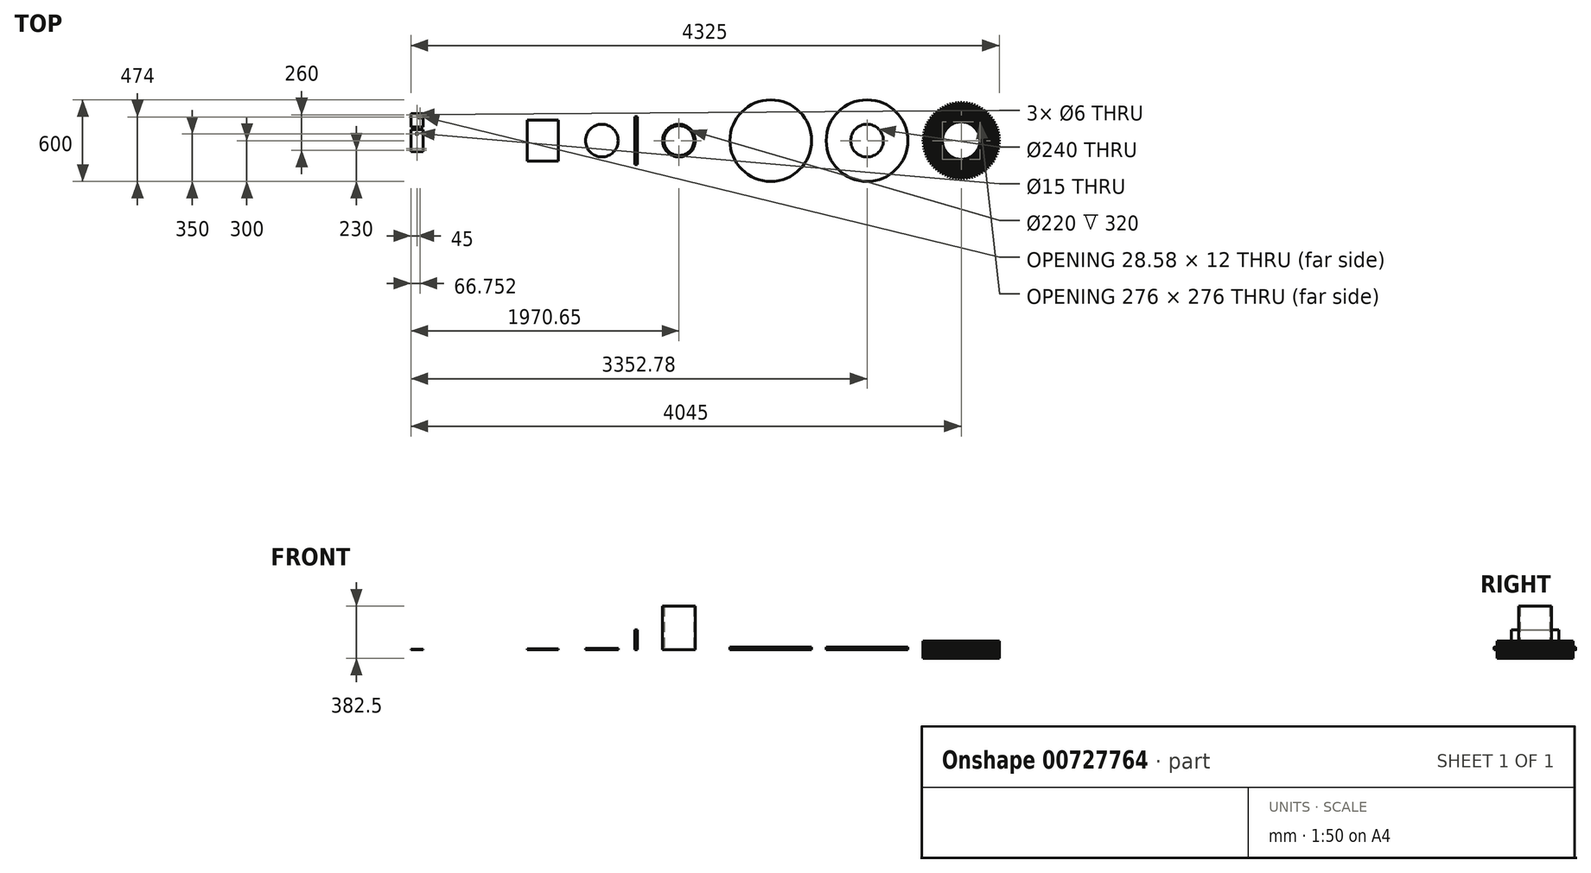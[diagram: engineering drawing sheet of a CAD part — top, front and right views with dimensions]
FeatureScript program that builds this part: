
annotation { "Feature Type Name" : "Feature", "Feature Type Description" : "" }
export const myFeature = defineFeature(function(context is Context, id is Id, definition is map)
    precondition{}
    {
        {
            var Q0;
            Q0=qCreatedBy(makeId("Top.planeOp"),FACE);
            var sketch = newSketch(context, id + "F0", { "sketchPlane" : qUnion([Q0])});
            skLineSegment(sketch, "E0.bottom", {"start": v(138, -5) * mm, "end": v(280, -5) * mm});
            skLineSegment(sketch, "E0.top", {"start": v(138, 5) * mm, "end": v(280, 5) * mm});
            skLineSegment(sketch, "E0.left", {"start": v(138, -5) * mm, "end": v(138, 5) * mm});
            skLineSegment(sketch, "E0.right", {"start": v(280, -5) * mm, "end": v(280, 5) * mm});
            skPoint(sketch, "E0.middle", {"position": v(209, 0) * mm});
            skLineSegment(sketch, "E1.1.0", {"start": v(137.3, 14.83) * mm, "end": v(278.93, 24.96) * mm});
            skLineSegment(sketch, "E1.1.1", {"start": v(138, 4.86) * mm, "end": v(137.3, 14.83) * mm});
            skLineSegment(sketch, "E1.1.2", {"start": v(138, 4.86) * mm, "end": v(279.64, 14.99) * mm});
            skLineSegment(sketch, "E1.1.3", {"start": v(279.64, 14.99) * mm, "end": v(278.93, 24.96) * mm});
            skLineSegment(sketch, "E1.2.0", {"start": v(135.88, 24.59) * mm, "end": v(276.44, 44.8) * mm});
            skLineSegment(sketch, "E1.2.1", {"start": v(137.3, 14.7) * mm, "end": v(135.88, 24.59) * mm});
            skLineSegment(sketch, "E1.2.2", {"start": v(137.3, 14.7) * mm, "end": v(277.86, 34.9) * mm});
            skLineSegment(sketch, "E1.2.3", {"start": v(277.86, 34.9) * mm, "end": v(276.44, 44.8) * mm});
            skLineSegment(sketch, "E1.3.0", {"start": v(133.78, 34.22) * mm, "end": v(272.54, 64.4) * mm});
            skLineSegment(sketch, "E1.3.1", {"start": v(135.9, 24.45) * mm, "end": v(133.78, 34.22) * mm});
            skLineSegment(sketch, "E1.3.2", {"start": v(135.9, 24.45) * mm, "end": v(274.66, 54.63) * mm});
            skLineSegment(sketch, "E1.3.3", {"start": v(274.66, 54.63) * mm, "end": v(272.54, 64.4) * mm});
            skLineSegment(sketch, "E1.4.0", {"start": v(131, 43.68) * mm, "end": v(267.25, 83.68) * mm});
            skLineSegment(sketch, "E1.4.1", {"start": v(133.82, 34.08) * mm, "end": v(131, 43.68) * mm});
            skLineSegment(sketch, "E1.4.2", {"start": v(133.82, 34.08) * mm, "end": v(270.07, 74.09) * mm});
            skLineSegment(sketch, "E1.4.3", {"start": v(270.07, 74.09) * mm, "end": v(267.25, 83.68) * mm});
            skLineSegment(sketch, "E1.5.0", {"start": v(127.55, 52.91) * mm, "end": v(260.6, 102.53) * mm});
            skLineSegment(sketch, "E1.5.1", {"start": v(131.05, 43.54) * mm, "end": v(127.55, 52.91) * mm});
            skLineSegment(sketch, "E1.5.2", {"start": v(131.05, 43.54) * mm, "end": v(264.1, 93.17) * mm});
            skLineSegment(sketch, "E1.5.3", {"start": v(264.1, 93.17) * mm, "end": v(260.6, 102.53) * mm});
            skLineSegment(sketch, "E1.6.0", {"start": v(123.45, 61.88) * mm, "end": v(252.62, 120.86) * mm});
            skLineSegment(sketch, "E1.6.1", {"start": v(127.6, 52.78) * mm, "end": v(123.45, 61.88) * mm});
            skLineSegment(sketch, "E1.6.2", {"start": v(127.6, 52.78) * mm, "end": v(256.77, 111.77) * mm});
            skLineSegment(sketch, "E1.6.3", {"start": v(256.77, 111.77) * mm, "end": v(252.62, 120.86) * mm});
            skLineSegment(sketch, "E1.7.0", {"start": v(118.72, 70.52) * mm, "end": v(243.35, 138.58) * mm});
            skLineSegment(sketch, "E1.7.1", {"start": v(123.52, 61.75) * mm, "end": v(118.72, 70.52) * mm});
            skLineSegment(sketch, "E1.7.2", {"start": v(123.52, 61.75) * mm, "end": v(248.15, 129.8) * mm});
            skLineSegment(sketch, "E1.7.3", {"start": v(248.15, 129.8) * mm, "end": v(243.35, 138.58) * mm});
            skLineSegment(sketch, "E1.8.0", {"start": v(113.39, 78.81) * mm, "end": v(232.85, 155.59) * mm});
            skLineSegment(sketch, "E1.8.1", {"start": v(118.8, 70.4) * mm, "end": v(113.39, 78.81) * mm});
            skLineSegment(sketch, "E1.8.2", {"start": v(118.8, 70.4) * mm, "end": v(238.25, 147.17) * mm});
            skLineSegment(sketch, "E1.8.3", {"start": v(238.25, 147.17) * mm, "end": v(232.85, 155.59) * mm});
            skLineSegment(sketch, "E1.9.0", {"start": v(107.48, 86.7) * mm, "end": v(221.16, 171.8) * mm});
            skLineSegment(sketch, "E1.9.1", {"start": v(113.47, 78.7) * mm, "end": v(107.48, 86.7) * mm});
            skLineSegment(sketch, "E1.9.2", {"start": v(113.47, 78.7) * mm, "end": v(227.15, 163.8) * mm});
            skLineSegment(sketch, "E1.9.3", {"start": v(227.15, 163.8) * mm, "end": v(221.16, 171.8) * mm});
            skLineSegment(sketch, "E1.10.0", {"start": v(101.02, 94.15) * mm, "end": v(208.34, 187.14) * mm});
            skLineSegment(sketch, "E1.10.1", {"start": v(107.57, 86.6) * mm, "end": v(101.02, 94.15) * mm});
            skLineSegment(sketch, "E1.10.2", {"start": v(107.57, 86.6) * mm, "end": v(214.88, 179.58) * mm});
            skLineSegment(sketch, "E1.10.3", {"start": v(214.88, 179.58) * mm, "end": v(208.34, 187.14) * mm});
            skLineSegment(sketch, "E1.11.0", {"start": v(94.05, 101.12) * mm, "end": v(194.45, 201.53) * mm});
            skLineSegment(sketch, "E1.11.1", {"start": v(101.12, 94.05) * mm, "end": v(94.05, 101.12) * mm});
            skLineSegment(sketch, "E1.11.2", {"start": v(101.12, 94.05) * mm, "end": v(201.53, 194.45) * mm});
            skLineSegment(sketch, "E1.11.3", {"start": v(201.53, 194.45) * mm, "end": v(194.45, 201.53) * mm});
            skLineSegment(sketch, "E1.12.0", {"start": v(86.6, 107.57) * mm, "end": v(179.58, 214.88) * mm});
            skLineSegment(sketch, "E1.12.1", {"start": v(94.15, 101.02) * mm, "end": v(86.6, 107.57) * mm});
            skLineSegment(sketch, "E1.12.2", {"start": v(94.15, 101.02) * mm, "end": v(187.14, 208.34) * mm});
            skLineSegment(sketch, "E1.12.3", {"start": v(187.14, 208.34) * mm, "end": v(179.58, 214.88) * mm});
            skLineSegment(sketch, "E1.13.0", {"start": v(78.7, 113.47) * mm, "end": v(163.8, 227.15) * mm});
            skLineSegment(sketch, "E1.13.1", {"start": v(86.7, 107.48) * mm, "end": v(78.7, 113.47) * mm});
            skLineSegment(sketch, "E1.13.2", {"start": v(86.7, 107.48) * mm, "end": v(171.8, 221.16) * mm});
            skLineSegment(sketch, "E1.13.3", {"start": v(171.8, 221.16) * mm, "end": v(163.8, 227.15) * mm});
            skLineSegment(sketch, "E1.14.0", {"start": v(70.4, 118.8) * mm, "end": v(147.17, 238.25) * mm});
            skLineSegment(sketch, "E1.14.1", {"start": v(78.81, 113.39) * mm, "end": v(70.4, 118.8) * mm});
            skLineSegment(sketch, "E1.14.2", {"start": v(78.81, 113.39) * mm, "end": v(155.59, 232.85) * mm});
            skLineSegment(sketch, "E1.14.3", {"start": v(155.59, 232.85) * mm, "end": v(147.17, 238.25) * mm});
            skLineSegment(sketch, "E1.15.0", {"start": v(61.75, 123.52) * mm, "end": v(129.8, 248.15) * mm});
            skLineSegment(sketch, "E1.15.1", {"start": v(70.52, 118.72) * mm, "end": v(61.75, 123.52) * mm});
            skLineSegment(sketch, "E1.15.2", {"start": v(70.52, 118.72) * mm, "end": v(138.58, 243.35) * mm});
            skLineSegment(sketch, "E1.15.3", {"start": v(138.58, 243.35) * mm, "end": v(129.8, 248.15) * mm});
            skLineSegment(sketch, "E1.16.0", {"start": v(52.78, 127.6) * mm, "end": v(111.77, 256.77) * mm});
            skLineSegment(sketch, "E1.16.1", {"start": v(61.88, 123.45) * mm, "end": v(52.78, 127.6) * mm});
            skLineSegment(sketch, "E1.16.2", {"start": v(61.88, 123.45) * mm, "end": v(120.86, 252.62) * mm});
            skLineSegment(sketch, "E1.16.3", {"start": v(120.86, 252.62) * mm, "end": v(111.77, 256.77) * mm});
            skLineSegment(sketch, "E1.17.0", {"start": v(43.54, 131.05) * mm, "end": v(93.17, 264.1) * mm});
            skLineSegment(sketch, "E1.17.1", {"start": v(52.91, 127.55) * mm, "end": v(43.54, 131.05) * mm});
            skLineSegment(sketch, "E1.17.2", {"start": v(52.91, 127.55) * mm, "end": v(102.53, 260.6) * mm});
            skLineSegment(sketch, "E1.17.3", {"start": v(102.53, 260.6) * mm, "end": v(93.17, 264.1) * mm});
            skLineSegment(sketch, "E1.18.0", {"start": v(34.08, 133.82) * mm, "end": v(74.09, 270.07) * mm});
            skLineSegment(sketch, "E1.18.1", {"start": v(43.68, 131) * mm, "end": v(34.08, 133.82) * mm});
            skLineSegment(sketch, "E1.18.2", {"start": v(43.68, 131) * mm, "end": v(83.68, 267.25) * mm});
            skLineSegment(sketch, "E1.18.3", {"start": v(83.68, 267.25) * mm, "end": v(74.09, 270.07) * mm});
            skLineSegment(sketch, "E1.19.0", {"start": v(24.45, 135.9) * mm, "end": v(54.63, 274.66) * mm});
            skLineSegment(sketch, "E1.19.1", {"start": v(34.22, 133.78) * mm, "end": v(24.45, 135.9) * mm});
            skLineSegment(sketch, "E1.19.2", {"start": v(34.22, 133.78) * mm, "end": v(64.4, 272.54) * mm});
            skLineSegment(sketch, "E1.19.3", {"start": v(64.4, 272.54) * mm, "end": v(54.63, 274.66) * mm});
            skLineSegment(sketch, "E1.20.0", {"start": v(14.7, 137.3) * mm, "end": v(34.9, 277.86) * mm});
            skLineSegment(sketch, "E1.20.1", {"start": v(24.59, 135.88) * mm, "end": v(14.7, 137.3) * mm});
            skLineSegment(sketch, "E1.20.2", {"start": v(24.59, 135.88) * mm, "end": v(44.8, 276.44) * mm});
            skLineSegment(sketch, "E1.20.3", {"start": v(44.8, 276.44) * mm, "end": v(34.9, 277.86) * mm});
            skLineSegment(sketch, "E1.21.0", {"start": v(4.86, 138) * mm, "end": v(14.99, 279.64) * mm});
            skLineSegment(sketch, "E1.21.1", {"start": v(14.83, 137.3) * mm, "end": v(4.86, 138) * mm});
            skLineSegment(sketch, "E1.21.2", {"start": v(14.83, 137.3) * mm, "end": v(24.96, 278.93) * mm});
            skLineSegment(sketch, "E1.21.3", {"start": v(24.96, 278.93) * mm, "end": v(14.99, 279.64) * mm});
            skLineSegment(sketch, "E1.22.0", {"start": v(-5, 138) * mm, "end": v(-5, 280) * mm});
            skLineSegment(sketch, "E1.22.1", {"start": v(5, 138) * mm, "end": v(-5, 138) * mm});
            skLineSegment(sketch, "E1.22.2", {"start": v(5, 138) * mm, "end": v(5, 280) * mm});
            skLineSegment(sketch, "E1.22.3", {"start": v(5, 280) * mm, "end": v(-5, 280) * mm});
            skLineSegment(sketch, "E1.23.0", {"start": v(-14.83, 137.3) * mm, "end": v(-24.96, 278.93) * mm});
            skLineSegment(sketch, "E1.23.1", {"start": v(-4.86, 138) * mm, "end": v(-14.83, 137.3) * mm});
            skLineSegment(sketch, "E1.23.2", {"start": v(-4.86, 138) * mm, "end": v(-14.99, 279.64) * mm});
            skLineSegment(sketch, "E1.23.3", {"start": v(-14.99, 279.64) * mm, "end": v(-24.96, 278.93) * mm});
            skLineSegment(sketch, "E1.24.0", {"start": v(-24.59, 135.88) * mm, "end": v(-44.8, 276.44) * mm});
            skLineSegment(sketch, "E1.24.1", {"start": v(-14.7, 137.3) * mm, "end": v(-24.59, 135.88) * mm});
            skLineSegment(sketch, "E1.24.2", {"start": v(-14.7, 137.3) * mm, "end": v(-34.9, 277.86) * mm});
            skLineSegment(sketch, "E1.24.3", {"start": v(-34.9, 277.86) * mm, "end": v(-44.8, 276.44) * mm});
            skLineSegment(sketch, "E1.25.0", {"start": v(-34.22, 133.78) * mm, "end": v(-64.4, 272.54) * mm});
            skLineSegment(sketch, "E1.25.1", {"start": v(-24.45, 135.9) * mm, "end": v(-34.22, 133.78) * mm});
            skLineSegment(sketch, "E1.25.2", {"start": v(-24.45, 135.9) * mm, "end": v(-54.63, 274.66) * mm});
            skLineSegment(sketch, "E1.25.3", {"start": v(-54.63, 274.66) * mm, "end": v(-64.4, 272.54) * mm});
            skLineSegment(sketch, "E1.26.0", {"start": v(-43.68, 131) * mm, "end": v(-83.68, 267.25) * mm});
            skLineSegment(sketch, "E1.26.1", {"start": v(-34.08, 133.82) * mm, "end": v(-43.68, 131) * mm});
            skLineSegment(sketch, "E1.26.2", {"start": v(-34.08, 133.82) * mm, "end": v(-74.09, 270.07) * mm});
            skLineSegment(sketch, "E1.26.3", {"start": v(-74.09, 270.07) * mm, "end": v(-83.68, 267.25) * mm});
            skLineSegment(sketch, "E1.27.0", {"start": v(-52.91, 127.55) * mm, "end": v(-102.53, 260.6) * mm});
            skLineSegment(sketch, "E1.27.1", {"start": v(-43.54, 131.05) * mm, "end": v(-52.91, 127.55) * mm});
            skLineSegment(sketch, "E1.27.2", {"start": v(-43.54, 131.05) * mm, "end": v(-93.17, 264.1) * mm});
            skLineSegment(sketch, "E1.27.3", {"start": v(-93.17, 264.1) * mm, "end": v(-102.53, 260.6) * mm});
            skLineSegment(sketch, "E1.28.0", {"start": v(-61.88, 123.45) * mm, "end": v(-120.86, 252.62) * mm});
            skLineSegment(sketch, "E1.28.1", {"start": v(-52.78, 127.6) * mm, "end": v(-61.88, 123.45) * mm});
            skLineSegment(sketch, "E1.28.2", {"start": v(-52.78, 127.6) * mm, "end": v(-111.77, 256.77) * mm});
            skLineSegment(sketch, "E1.28.3", {"start": v(-111.77, 256.77) * mm, "end": v(-120.86, 252.62) * mm});
            skLineSegment(sketch, "E1.29.0", {"start": v(-70.52, 118.72) * mm, "end": v(-138.58, 243.35) * mm});
            skLineSegment(sketch, "E1.29.1", {"start": v(-61.75, 123.52) * mm, "end": v(-70.52, 118.72) * mm});
            skLineSegment(sketch, "E1.29.2", {"start": v(-61.75, 123.52) * mm, "end": v(-129.8, 248.15) * mm});
            skLineSegment(sketch, "E1.29.3", {"start": v(-129.8, 248.15) * mm, "end": v(-138.58, 243.35) * mm});
            skLineSegment(sketch, "E1.30.0", {"start": v(-78.81, 113.39) * mm, "end": v(-155.59, 232.85) * mm});
            skLineSegment(sketch, "E1.30.1", {"start": v(-70.4, 118.8) * mm, "end": v(-78.81, 113.39) * mm});
            skLineSegment(sketch, "E1.30.2", {"start": v(-70.4, 118.8) * mm, "end": v(-147.17, 238.25) * mm});
            skLineSegment(sketch, "E1.30.3", {"start": v(-147.17, 238.25) * mm, "end": v(-155.59, 232.85) * mm});
            skLineSegment(sketch, "E1.31.0", {"start": v(-86.7, 107.48) * mm, "end": v(-171.8, 221.16) * mm});
            skLineSegment(sketch, "E1.31.1", {"start": v(-78.7, 113.47) * mm, "end": v(-86.7, 107.48) * mm});
            skLineSegment(sketch, "E1.31.2", {"start": v(-78.7, 113.47) * mm, "end": v(-163.8, 227.15) * mm});
            skLineSegment(sketch, "E1.31.3", {"start": v(-163.8, 227.15) * mm, "end": v(-171.8, 221.16) * mm});
            skLineSegment(sketch, "E1.32.0", {"start": v(-94.15, 101.02) * mm, "end": v(-187.14, 208.34) * mm});
            skLineSegment(sketch, "E1.32.1", {"start": v(-86.6, 107.57) * mm, "end": v(-94.15, 101.02) * mm});
            skLineSegment(sketch, "E1.32.2", {"start": v(-86.6, 107.57) * mm, "end": v(-179.58, 214.88) * mm});
            skLineSegment(sketch, "E1.32.3", {"start": v(-179.58, 214.88) * mm, "end": v(-187.14, 208.34) * mm});
            skLineSegment(sketch, "E1.33.0", {"start": v(-101.12, 94.05) * mm, "end": v(-201.53, 194.45) * mm});
            skLineSegment(sketch, "E1.33.1", {"start": v(-94.05, 101.12) * mm, "end": v(-101.12, 94.05) * mm});
            skLineSegment(sketch, "E1.33.2", {"start": v(-94.05, 101.12) * mm, "end": v(-194.45, 201.53) * mm});
            skLineSegment(sketch, "E1.33.3", {"start": v(-194.45, 201.53) * mm, "end": v(-201.53, 194.45) * mm});
            skLineSegment(sketch, "E1.34.0", {"start": v(-107.57, 86.6) * mm, "end": v(-214.88, 179.58) * mm});
            skLineSegment(sketch, "E1.34.1", {"start": v(-101.02, 94.15) * mm, "end": v(-107.57, 86.6) * mm});
            skLineSegment(sketch, "E1.34.2", {"start": v(-101.02, 94.15) * mm, "end": v(-208.34, 187.14) * mm});
            skLineSegment(sketch, "E1.34.3", {"start": v(-208.34, 187.14) * mm, "end": v(-214.88, 179.58) * mm});
            skLineSegment(sketch, "E1.35.0", {"start": v(-113.47, 78.7) * mm, "end": v(-227.15, 163.8) * mm});
            skLineSegment(sketch, "E1.35.1", {"start": v(-107.48, 86.7) * mm, "end": v(-113.47, 78.7) * mm});
            skLineSegment(sketch, "E1.35.2", {"start": v(-107.48, 86.7) * mm, "end": v(-221.16, 171.8) * mm});
            skLineSegment(sketch, "E1.35.3", {"start": v(-221.16, 171.8) * mm, "end": v(-227.15, 163.8) * mm});
            skLineSegment(sketch, "E1.36.0", {"start": v(-118.8, 70.4) * mm, "end": v(-238.25, 147.17) * mm});
            skLineSegment(sketch, "E1.36.1", {"start": v(-113.39, 78.81) * mm, "end": v(-118.8, 70.4) * mm});
            skLineSegment(sketch, "E1.36.2", {"start": v(-113.39, 78.81) * mm, "end": v(-232.85, 155.59) * mm});
            skLineSegment(sketch, "E1.36.3", {"start": v(-232.85, 155.59) * mm, "end": v(-238.25, 147.17) * mm});
            skLineSegment(sketch, "E1.37.0", {"start": v(-123.52, 61.75) * mm, "end": v(-248.15, 129.8) * mm});
            skLineSegment(sketch, "E1.37.1", {"start": v(-118.72, 70.52) * mm, "end": v(-123.52, 61.75) * mm});
            skLineSegment(sketch, "E1.37.2", {"start": v(-118.72, 70.52) * mm, "end": v(-243.35, 138.58) * mm});
            skLineSegment(sketch, "E1.37.3", {"start": v(-243.35, 138.58) * mm, "end": v(-248.15, 129.8) * mm});
            skLineSegment(sketch, "E1.38.0", {"start": v(-127.6, 52.78) * mm, "end": v(-256.77, 111.77) * mm});
            skLineSegment(sketch, "E1.38.1", {"start": v(-123.45, 61.88) * mm, "end": v(-127.6, 52.78) * mm});
            skLineSegment(sketch, "E1.38.2", {"start": v(-123.45, 61.88) * mm, "end": v(-252.62, 120.86) * mm});
            skLineSegment(sketch, "E1.38.3", {"start": v(-252.62, 120.86) * mm, "end": v(-256.77, 111.77) * mm});
            skLineSegment(sketch, "E1.39.0", {"start": v(-131.05, 43.54) * mm, "end": v(-264.1, 93.17) * mm});
            skLineSegment(sketch, "E1.39.1", {"start": v(-127.55, 52.91) * mm, "end": v(-131.05, 43.54) * mm});
            skLineSegment(sketch, "E1.39.2", {"start": v(-127.55, 52.91) * mm, "end": v(-260.6, 102.53) * mm});
            skLineSegment(sketch, "E1.39.3", {"start": v(-260.6, 102.53) * mm, "end": v(-264.1, 93.17) * mm});
            skLineSegment(sketch, "E1.40.0", {"start": v(-133.82, 34.08) * mm, "end": v(-270.07, 74.09) * mm});
            skLineSegment(sketch, "E1.40.1", {"start": v(-131, 43.68) * mm, "end": v(-133.82, 34.08) * mm});
            skLineSegment(sketch, "E1.40.2", {"start": v(-131, 43.68) * mm, "end": v(-267.25, 83.68) * mm});
            skLineSegment(sketch, "E1.40.3", {"start": v(-267.25, 83.68) * mm, "end": v(-270.07, 74.09) * mm});
            skLineSegment(sketch, "E1.41.0", {"start": v(-135.9, 24.45) * mm, "end": v(-274.66, 54.63) * mm});
            skLineSegment(sketch, "E1.41.1", {"start": v(-133.78, 34.22) * mm, "end": v(-135.9, 24.45) * mm});
            skLineSegment(sketch, "E1.41.2", {"start": v(-133.78, 34.22) * mm, "end": v(-272.54, 64.4) * mm});
            skLineSegment(sketch, "E1.41.3", {"start": v(-272.54, 64.4) * mm, "end": v(-274.66, 54.63) * mm});
            skLineSegment(sketch, "E1.42.0", {"start": v(-137.3, 14.7) * mm, "end": v(-277.86, 34.9) * mm});
            skLineSegment(sketch, "E1.42.1", {"start": v(-135.88, 24.59) * mm, "end": v(-137.3, 14.7) * mm});
            skLineSegment(sketch, "E1.42.2", {"start": v(-135.88, 24.59) * mm, "end": v(-276.44, 44.8) * mm});
            skLineSegment(sketch, "E1.42.3", {"start": v(-276.44, 44.8) * mm, "end": v(-277.86, 34.9) * mm});
            skLineSegment(sketch, "E1.43.0", {"start": v(-138, 4.86) * mm, "end": v(-279.64, 14.99) * mm});
            skLineSegment(sketch, "E1.43.1", {"start": v(-137.3, 14.83) * mm, "end": v(-138, 4.86) * mm});
            skLineSegment(sketch, "E1.43.2", {"start": v(-137.3, 14.83) * mm, "end": v(-278.93, 24.96) * mm});
            skLineSegment(sketch, "E1.43.3", {"start": v(-278.93, 24.96) * mm, "end": v(-279.64, 14.99) * mm});
            skLineSegment(sketch, "E1.44.0", {"start": v(-138, -5) * mm, "end": v(-280, -5) * mm});
            skLineSegment(sketch, "E1.44.1", {"start": v(-138, 5) * mm, "end": v(-138, -5) * mm});
            skLineSegment(sketch, "E1.44.2", {"start": v(-138, 5) * mm, "end": v(-280, 5) * mm});
            skLineSegment(sketch, "E1.44.3", {"start": v(-280, 5) * mm, "end": v(-280, -5) * mm});
            skLineSegment(sketch, "E1.45.0", {"start": v(-137.3, -14.83) * mm, "end": v(-278.93, -24.96) * mm});
            skLineSegment(sketch, "E1.45.1", {"start": v(-138, -4.86) * mm, "end": v(-137.3, -14.83) * mm});
            skLineSegment(sketch, "E1.45.2", {"start": v(-138, -4.86) * mm, "end": v(-279.64, -14.99) * mm});
            skLineSegment(sketch, "E1.45.3", {"start": v(-279.64, -14.99) * mm, "end": v(-278.93, -24.96) * mm});
            skLineSegment(sketch, "E1.46.0", {"start": v(-135.88, -24.59) * mm, "end": v(-276.44, -44.8) * mm});
            skLineSegment(sketch, "E1.46.1", {"start": v(-137.3, -14.7) * mm, "end": v(-135.88, -24.59) * mm});
            skLineSegment(sketch, "E1.46.2", {"start": v(-137.3, -14.7) * mm, "end": v(-277.86, -34.9) * mm});
            skLineSegment(sketch, "E1.46.3", {"start": v(-277.86, -34.9) * mm, "end": v(-276.44, -44.8) * mm});
            skLineSegment(sketch, "E1.47.0", {"start": v(-133.78, -34.22) * mm, "end": v(-272.54, -64.4) * mm});
            skLineSegment(sketch, "E1.47.1", {"start": v(-135.9, -24.45) * mm, "end": v(-133.78, -34.22) * mm});
            skLineSegment(sketch, "E1.47.2", {"start": v(-135.9, -24.45) * mm, "end": v(-274.66, -54.63) * mm});
            skLineSegment(sketch, "E1.47.3", {"start": v(-274.66, -54.63) * mm, "end": v(-272.54, -64.4) * mm});
            skLineSegment(sketch, "E1.48.0", {"start": v(-131, -43.68) * mm, "end": v(-267.25, -83.68) * mm});
            skLineSegment(sketch, "E1.48.1", {"start": v(-133.82, -34.08) * mm, "end": v(-131, -43.68) * mm});
            skLineSegment(sketch, "E1.48.2", {"start": v(-133.82, -34.08) * mm, "end": v(-270.07, -74.09) * mm});
            skLineSegment(sketch, "E1.48.3", {"start": v(-270.07, -74.09) * mm, "end": v(-267.25, -83.68) * mm});
            skLineSegment(sketch, "E1.49.0", {"start": v(-127.55, -52.91) * mm, "end": v(-260.6, -102.53) * mm});
            skLineSegment(sketch, "E1.49.1", {"start": v(-131.05, -43.54) * mm, "end": v(-127.55, -52.91) * mm});
            skLineSegment(sketch, "E1.49.2", {"start": v(-131.05, -43.54) * mm, "end": v(-264.1, -93.17) * mm});
            skLineSegment(sketch, "E1.49.3", {"start": v(-264.1, -93.17) * mm, "end": v(-260.6, -102.53) * mm});
            skLineSegment(sketch, "E1.50.0", {"start": v(-123.45, -61.88) * mm, "end": v(-252.62, -120.86) * mm});
            skLineSegment(sketch, "E1.50.1", {"start": v(-127.6, -52.78) * mm, "end": v(-123.45, -61.88) * mm});
            skLineSegment(sketch, "E1.50.2", {"start": v(-127.6, -52.78) * mm, "end": v(-256.77, -111.77) * mm});
            skLineSegment(sketch, "E1.50.3", {"start": v(-256.77, -111.77) * mm, "end": v(-252.62, -120.86) * mm});
            skLineSegment(sketch, "E1.51.0", {"start": v(-118.72, -70.52) * mm, "end": v(-243.35, -138.58) * mm});
            skLineSegment(sketch, "E1.51.1", {"start": v(-123.52, -61.75) * mm, "end": v(-118.72, -70.52) * mm});
            skLineSegment(sketch, "E1.51.2", {"start": v(-123.52, -61.75) * mm, "end": v(-248.15, -129.8) * mm});
            skLineSegment(sketch, "E1.51.3", {"start": v(-248.15, -129.8) * mm, "end": v(-243.35, -138.58) * mm});
            skLineSegment(sketch, "E1.52.0", {"start": v(-113.39, -78.81) * mm, "end": v(-232.85, -155.59) * mm});
            skLineSegment(sketch, "E1.52.1", {"start": v(-118.8, -70.4) * mm, "end": v(-113.39, -78.81) * mm});
            skLineSegment(sketch, "E1.52.2", {"start": v(-118.8, -70.4) * mm, "end": v(-238.25, -147.17) * mm});
            skLineSegment(sketch, "E1.52.3", {"start": v(-238.25, -147.17) * mm, "end": v(-232.85, -155.59) * mm});
            skLineSegment(sketch, "E1.53.0", {"start": v(-107.48, -86.7) * mm, "end": v(-221.16, -171.8) * mm});
            skLineSegment(sketch, "E1.53.1", {"start": v(-113.47, -78.7) * mm, "end": v(-107.48, -86.7) * mm});
            skLineSegment(sketch, "E1.53.2", {"start": v(-113.47, -78.7) * mm, "end": v(-227.15, -163.8) * mm});
            skLineSegment(sketch, "E1.53.3", {"start": v(-227.15, -163.8) * mm, "end": v(-221.16, -171.8) * mm});
            skLineSegment(sketch, "E1.54.0", {"start": v(-101.02, -94.15) * mm, "end": v(-208.34, -187.14) * mm});
            skLineSegment(sketch, "E1.54.1", {"start": v(-107.57, -86.6) * mm, "end": v(-101.02, -94.15) * mm});
            skLineSegment(sketch, "E1.54.2", {"start": v(-107.57, -86.6) * mm, "end": v(-214.88, -179.58) * mm});
            skLineSegment(sketch, "E1.54.3", {"start": v(-214.88, -179.58) * mm, "end": v(-208.34, -187.14) * mm});
            skLineSegment(sketch, "E1.55.0", {"start": v(-94.05, -101.12) * mm, "end": v(-194.45, -201.53) * mm});
            skLineSegment(sketch, "E1.55.1", {"start": v(-101.12, -94.05) * mm, "end": v(-94.05, -101.12) * mm});
            skLineSegment(sketch, "E1.55.2", {"start": v(-101.12, -94.05) * mm, "end": v(-201.53, -194.45) * mm});
            skLineSegment(sketch, "E1.55.3", {"start": v(-201.53, -194.45) * mm, "end": v(-194.45, -201.53) * mm});
            skLineSegment(sketch, "E1.56.0", {"start": v(-86.6, -107.57) * mm, "end": v(-179.58, -214.88) * mm});
            skLineSegment(sketch, "E1.56.1", {"start": v(-94.15, -101.02) * mm, "end": v(-86.6, -107.57) * mm});
            skLineSegment(sketch, "E1.56.2", {"start": v(-94.15, -101.02) * mm, "end": v(-187.14, -208.34) * mm});
            skLineSegment(sketch, "E1.56.3", {"start": v(-187.14, -208.34) * mm, "end": v(-179.58, -214.88) * mm});
            skLineSegment(sketch, "E1.57.0", {"start": v(-78.7, -113.47) * mm, "end": v(-163.8, -227.15) * mm});
            skLineSegment(sketch, "E1.57.1", {"start": v(-86.7, -107.48) * mm, "end": v(-78.7, -113.47) * mm});
            skLineSegment(sketch, "E1.57.2", {"start": v(-86.7, -107.48) * mm, "end": v(-171.8, -221.16) * mm});
            skLineSegment(sketch, "E1.57.3", {"start": v(-171.8, -221.16) * mm, "end": v(-163.8, -227.15) * mm});
            skLineSegment(sketch, "E1.58.0", {"start": v(-70.4, -118.8) * mm, "end": v(-147.17, -238.25) * mm});
            skLineSegment(sketch, "E1.58.1", {"start": v(-78.81, -113.39) * mm, "end": v(-70.4, -118.8) * mm});
            skLineSegment(sketch, "E1.58.2", {"start": v(-78.81, -113.39) * mm, "end": v(-155.59, -232.85) * mm});
            skLineSegment(sketch, "E1.58.3", {"start": v(-155.59, -232.85) * mm, "end": v(-147.17, -238.25) * mm});
            skLineSegment(sketch, "E1.59.0", {"start": v(-61.75, -123.52) * mm, "end": v(-129.8, -248.15) * mm});
            skLineSegment(sketch, "E1.59.1", {"start": v(-70.52, -118.72) * mm, "end": v(-61.75, -123.52) * mm});
            skLineSegment(sketch, "E1.59.2", {"start": v(-70.52, -118.72) * mm, "end": v(-138.58, -243.35) * mm});
            skLineSegment(sketch, "E1.59.3", {"start": v(-138.58, -243.35) * mm, "end": v(-129.8, -248.15) * mm});
            skLineSegment(sketch, "E1.60.0", {"start": v(-52.78, -127.6) * mm, "end": v(-111.77, -256.77) * mm});
            skLineSegment(sketch, "E1.60.1", {"start": v(-61.88, -123.45) * mm, "end": v(-52.78, -127.6) * mm});
            skLineSegment(sketch, "E1.60.2", {"start": v(-61.88, -123.45) * mm, "end": v(-120.86, -252.62) * mm});
            skLineSegment(sketch, "E1.60.3", {"start": v(-120.86, -252.62) * mm, "end": v(-111.77, -256.77) * mm});
            skLineSegment(sketch, "E1.61.0", {"start": v(-43.54, -131.05) * mm, "end": v(-93.17, -264.1) * mm});
            skLineSegment(sketch, "E1.61.1", {"start": v(-52.91, -127.55) * mm, "end": v(-43.54, -131.05) * mm});
            skLineSegment(sketch, "E1.61.2", {"start": v(-52.91, -127.55) * mm, "end": v(-102.53, -260.6) * mm});
            skLineSegment(sketch, "E1.61.3", {"start": v(-102.53, -260.6) * mm, "end": v(-93.17, -264.1) * mm});
            skLineSegment(sketch, "E1.62.0", {"start": v(-34.08, -133.82) * mm, "end": v(-74.09, -270.07) * mm});
            skLineSegment(sketch, "E1.62.1", {"start": v(-43.68, -131) * mm, "end": v(-34.08, -133.82) * mm});
            skLineSegment(sketch, "E1.62.2", {"start": v(-43.68, -131) * mm, "end": v(-83.68, -267.25) * mm});
            skLineSegment(sketch, "E1.62.3", {"start": v(-83.68, -267.25) * mm, "end": v(-74.09, -270.07) * mm});
            skLineSegment(sketch, "E1.63.0", {"start": v(-24.45, -135.9) * mm, "end": v(-54.63, -274.66) * mm});
            skLineSegment(sketch, "E1.63.1", {"start": v(-34.22, -133.78) * mm, "end": v(-24.45, -135.9) * mm});
            skLineSegment(sketch, "E1.63.2", {"start": v(-34.22, -133.78) * mm, "end": v(-64.4, -272.54) * mm});
            skLineSegment(sketch, "E1.63.3", {"start": v(-64.4, -272.54) * mm, "end": v(-54.63, -274.66) * mm});
            skLineSegment(sketch, "E1.64.0", {"start": v(-14.7, -137.3) * mm, "end": v(-34.9, -277.86) * mm});
            skLineSegment(sketch, "E1.64.1", {"start": v(-24.59, -135.88) * mm, "end": v(-14.7, -137.3) * mm});
            skLineSegment(sketch, "E1.64.2", {"start": v(-24.59, -135.88) * mm, "end": v(-44.8, -276.44) * mm});
            skLineSegment(sketch, "E1.64.3", {"start": v(-44.8, -276.44) * mm, "end": v(-34.9, -277.86) * mm});
            skLineSegment(sketch, "E1.65.0", {"start": v(-4.86, -138) * mm, "end": v(-14.99, -279.64) * mm});
            skLineSegment(sketch, "E1.65.1", {"start": v(-14.83, -137.3) * mm, "end": v(-4.86, -138) * mm});
            skLineSegment(sketch, "E1.65.2", {"start": v(-14.83, -137.3) * mm, "end": v(-24.96, -278.93) * mm});
            skLineSegment(sketch, "E1.65.3", {"start": v(-24.96, -278.93) * mm, "end": v(-14.99, -279.64) * mm});
            skLineSegment(sketch, "E1.66.0", {"start": v(5, -138) * mm, "end": v(5, -280) * mm});
            skLineSegment(sketch, "E1.66.1", {"start": v(-5, -138) * mm, "end": v(5, -138) * mm});
            skLineSegment(sketch, "E1.66.2", {"start": v(-5, -138) * mm, "end": v(-5, -280) * mm});
            skLineSegment(sketch, "E1.66.3", {"start": v(-5, -280) * mm, "end": v(5, -280) * mm});
            skLineSegment(sketch, "E1.67.0", {"start": v(14.83, -137.3) * mm, "end": v(24.96, -278.93) * mm});
            skLineSegment(sketch, "E1.67.1", {"start": v(4.86, -138) * mm, "end": v(14.83, -137.3) * mm});
            skLineSegment(sketch, "E1.67.2", {"start": v(4.86, -138) * mm, "end": v(14.99, -279.64) * mm});
            skLineSegment(sketch, "E1.67.3", {"start": v(14.99, -279.64) * mm, "end": v(24.96, -278.93) * mm});
            skLineSegment(sketch, "E1.68.0", {"start": v(24.59, -135.88) * mm, "end": v(44.8, -276.44) * mm});
            skLineSegment(sketch, "E1.68.1", {"start": v(14.7, -137.3) * mm, "end": v(24.59, -135.88) * mm});
            skLineSegment(sketch, "E1.68.2", {"start": v(14.7, -137.3) * mm, "end": v(34.9, -277.86) * mm});
            skLineSegment(sketch, "E1.68.3", {"start": v(34.9, -277.86) * mm, "end": v(44.8, -276.44) * mm});
            skLineSegment(sketch, "E1.69.0", {"start": v(34.22, -133.78) * mm, "end": v(64.4, -272.54) * mm});
            skLineSegment(sketch, "E1.69.1", {"start": v(24.45, -135.9) * mm, "end": v(34.22, -133.78) * mm});
            skLineSegment(sketch, "E1.69.2", {"start": v(24.45, -135.9) * mm, "end": v(54.63, -274.66) * mm});
            skLineSegment(sketch, "E1.69.3", {"start": v(54.63, -274.66) * mm, "end": v(64.4, -272.54) * mm});
            skLineSegment(sketch, "E1.70.0", {"start": v(43.68, -131) * mm, "end": v(83.68, -267.25) * mm});
            skLineSegment(sketch, "E1.70.1", {"start": v(34.08, -133.82) * mm, "end": v(43.68, -131) * mm});
            skLineSegment(sketch, "E1.70.2", {"start": v(34.08, -133.82) * mm, "end": v(74.09, -270.07) * mm});
            skLineSegment(sketch, "E1.70.3", {"start": v(74.09, -270.07) * mm, "end": v(83.68, -267.25) * mm});
            skLineSegment(sketch, "E1.71.0", {"start": v(52.91, -127.55) * mm, "end": v(102.53, -260.6) * mm});
            skLineSegment(sketch, "E1.71.1", {"start": v(43.54, -131.05) * mm, "end": v(52.91, -127.55) * mm});
            skLineSegment(sketch, "E1.71.2", {"start": v(43.54, -131.05) * mm, "end": v(93.17, -264.1) * mm});
            skLineSegment(sketch, "E1.71.3", {"start": v(93.17, -264.1) * mm, "end": v(102.53, -260.6) * mm});
            skLineSegment(sketch, "E1.72.0", {"start": v(61.88, -123.45) * mm, "end": v(120.86, -252.62) * mm});
            skLineSegment(sketch, "E1.72.1", {"start": v(52.78, -127.6) * mm, "end": v(61.88, -123.45) * mm});
            skLineSegment(sketch, "E1.72.2", {"start": v(52.78, -127.6) * mm, "end": v(111.77, -256.77) * mm});
            skLineSegment(sketch, "E1.72.3", {"start": v(111.77, -256.77) * mm, "end": v(120.86, -252.62) * mm});
            skLineSegment(sketch, "E1.73.0", {"start": v(70.52, -118.72) * mm, "end": v(138.58, -243.35) * mm});
            skLineSegment(sketch, "E1.73.1", {"start": v(61.75, -123.52) * mm, "end": v(70.52, -118.72) * mm});
            skLineSegment(sketch, "E1.73.2", {"start": v(61.75, -123.52) * mm, "end": v(129.8, -248.15) * mm});
            skLineSegment(sketch, "E1.73.3", {"start": v(129.8, -248.15) * mm, "end": v(138.58, -243.35) * mm});
            skLineSegment(sketch, "E1.74.0", {"start": v(78.81, -113.39) * mm, "end": v(155.59, -232.85) * mm});
            skLineSegment(sketch, "E1.74.1", {"start": v(70.4, -118.8) * mm, "end": v(78.81, -113.39) * mm});
            skLineSegment(sketch, "E1.74.2", {"start": v(70.4, -118.8) * mm, "end": v(147.17, -238.25) * mm});
            skLineSegment(sketch, "E1.74.3", {"start": v(147.17, -238.25) * mm, "end": v(155.59, -232.85) * mm});
            skLineSegment(sketch, "E1.75.0", {"start": v(86.7, -107.48) * mm, "end": v(171.8, -221.16) * mm});
            skLineSegment(sketch, "E1.75.1", {"start": v(78.7, -113.47) * mm, "end": v(86.7, -107.48) * mm});
            skLineSegment(sketch, "E1.75.2", {"start": v(78.7, -113.47) * mm, "end": v(163.8, -227.15) * mm});
            skLineSegment(sketch, "E1.75.3", {"start": v(163.8, -227.15) * mm, "end": v(171.8, -221.16) * mm});
            skLineSegment(sketch, "E1.76.0", {"start": v(94.15, -101.02) * mm, "end": v(187.14, -208.34) * mm});
            skLineSegment(sketch, "E1.76.1", {"start": v(86.6, -107.57) * mm, "end": v(94.15, -101.02) * mm});
            skLineSegment(sketch, "E1.76.2", {"start": v(86.6, -107.57) * mm, "end": v(179.58, -214.88) * mm});
            skLineSegment(sketch, "E1.76.3", {"start": v(179.58, -214.88) * mm, "end": v(187.14, -208.34) * mm});
            skLineSegment(sketch, "E1.77.0", {"start": v(101.12, -94.05) * mm, "end": v(201.53, -194.45) * mm});
            skLineSegment(sketch, "E1.77.1", {"start": v(94.05, -101.12) * mm, "end": v(101.12, -94.05) * mm});
            skLineSegment(sketch, "E1.77.2", {"start": v(94.05, -101.12) * mm, "end": v(194.45, -201.53) * mm});
            skLineSegment(sketch, "E1.77.3", {"start": v(194.45, -201.53) * mm, "end": v(201.53, -194.45) * mm});
            skLineSegment(sketch, "E1.78.0", {"start": v(107.57, -86.6) * mm, "end": v(214.88, -179.58) * mm});
            skLineSegment(sketch, "E1.78.1", {"start": v(101.02, -94.15) * mm, "end": v(107.57, -86.6) * mm});
            skLineSegment(sketch, "E1.78.2", {"start": v(101.02, -94.15) * mm, "end": v(208.34, -187.14) * mm});
            skLineSegment(sketch, "E1.78.3", {"start": v(208.34, -187.14) * mm, "end": v(214.88, -179.58) * mm});
            skLineSegment(sketch, "E1.79.0", {"start": v(113.47, -78.7) * mm, "end": v(227.15, -163.8) * mm});
            skLineSegment(sketch, "E1.79.1", {"start": v(107.48, -86.7) * mm, "end": v(113.47, -78.7) * mm});
            skLineSegment(sketch, "E1.79.2", {"start": v(107.48, -86.7) * mm, "end": v(221.16, -171.8) * mm});
            skLineSegment(sketch, "E1.79.3", {"start": v(221.16, -171.8) * mm, "end": v(227.15, -163.8) * mm});
            skLineSegment(sketch, "E1.80.0", {"start": v(118.8, -70.4) * mm, "end": v(238.25, -147.17) * mm});
            skLineSegment(sketch, "E1.80.1", {"start": v(113.39, -78.81) * mm, "end": v(118.8, -70.4) * mm});
            skLineSegment(sketch, "E1.80.2", {"start": v(113.39, -78.81) * mm, "end": v(232.85, -155.59) * mm});
            skLineSegment(sketch, "E1.80.3", {"start": v(232.85, -155.59) * mm, "end": v(238.25, -147.17) * mm});
            skLineSegment(sketch, "E1.81.0", {"start": v(123.52, -61.75) * mm, "end": v(248.15, -129.8) * mm});
            skLineSegment(sketch, "E1.81.1", {"start": v(118.72, -70.52) * mm, "end": v(123.52, -61.75) * mm});
            skLineSegment(sketch, "E1.81.2", {"start": v(118.72, -70.52) * mm, "end": v(243.35, -138.58) * mm});
            skLineSegment(sketch, "E1.81.3", {"start": v(243.35, -138.58) * mm, "end": v(248.15, -129.8) * mm});
            skLineSegment(sketch, "E1.82.0", {"start": v(127.6, -52.78) * mm, "end": v(256.77, -111.77) * mm});
            skLineSegment(sketch, "E1.82.1", {"start": v(123.45, -61.88) * mm, "end": v(127.6, -52.78) * mm});
            skLineSegment(sketch, "E1.82.2", {"start": v(123.45, -61.88) * mm, "end": v(252.62, -120.86) * mm});
            skLineSegment(sketch, "E1.82.3", {"start": v(252.62, -120.86) * mm, "end": v(256.77, -111.77) * mm});
            skLineSegment(sketch, "E1.83.0", {"start": v(131.05, -43.54) * mm, "end": v(264.1, -93.17) * mm});
            skLineSegment(sketch, "E1.83.1", {"start": v(127.55, -52.91) * mm, "end": v(131.05, -43.54) * mm});
            skLineSegment(sketch, "E1.83.2", {"start": v(127.55, -52.91) * mm, "end": v(260.6, -102.53) * mm});
            skLineSegment(sketch, "E1.83.3", {"start": v(260.6, -102.53) * mm, "end": v(264.1, -93.17) * mm});
            skLineSegment(sketch, "E1.84.0", {"start": v(133.82, -34.08) * mm, "end": v(270.07, -74.09) * mm});
            skLineSegment(sketch, "E1.84.1", {"start": v(131, -43.68) * mm, "end": v(133.82, -34.08) * mm});
            skLineSegment(sketch, "E1.84.2", {"start": v(131, -43.68) * mm, "end": v(267.25, -83.68) * mm});
            skLineSegment(sketch, "E1.84.3", {"start": v(267.25, -83.68) * mm, "end": v(270.07, -74.09) * mm});
            skLineSegment(sketch, "E1.85.0", {"start": v(135.9, -24.45) * mm, "end": v(274.66, -54.63) * mm});
            skLineSegment(sketch, "E1.85.1", {"start": v(133.78, -34.22) * mm, "end": v(135.9, -24.45) * mm});
            skLineSegment(sketch, "E1.85.2", {"start": v(133.78, -34.22) * mm, "end": v(272.54, -64.4) * mm});
            skLineSegment(sketch, "E1.85.3", {"start": v(272.54, -64.4) * mm, "end": v(274.66, -54.63) * mm});
            skLineSegment(sketch, "E1.86.0", {"start": v(137.3, -14.7) * mm, "end": v(277.86, -34.9) * mm});
            skLineSegment(sketch, "E1.86.1", {"start": v(135.88, -24.59) * mm, "end": v(137.3, -14.7) * mm});
            skLineSegment(sketch, "E1.86.2", {"start": v(135.88, -24.59) * mm, "end": v(276.44, -44.8) * mm});
            skLineSegment(sketch, "E1.86.3", {"start": v(276.44, -44.8) * mm, "end": v(277.86, -34.9) * mm});
            skLineSegment(sketch, "E1.87.0", {"start": v(138, -4.86) * mm, "end": v(279.64, -14.99) * mm});
            skLineSegment(sketch, "E1.87.1", {"start": v(137.3, -14.83) * mm, "end": v(138, -4.86) * mm});
            skLineSegment(sketch, "E1.87.2", {"start": v(137.3, -14.83) * mm, "end": v(278.93, -24.96) * mm});
            skLineSegment(sketch, "E1.87.3", {"start": v(278.93, -24.96) * mm, "end": v(279.64, -14.99) * mm});
            skPoint(sketch, "E1.center", {"position": v(0, 0) * mm});
            skSolve(sketch);
        }
        {
            var Q0;
            Q0 = qSketchRegion(id + "F0", true);
            extrude(context, id + "F1", {"entities" : qUnion([Q0]), "depth" : 125 * mm, "offsetDistance" : 25 * mm, "symmetric" : true});
        }
        {
            var Q0;
            Q0=qCreatedBy(makeId("Top.planeOp"),FACE);
            var sketch = newSketch(context, id + "F2", { "sketchPlane" : qUnion([Q0])});
            skCircle(sketch, "E2", {"center": v(-692.22, 0) * mm, "radius": 300 * mm});
            skSolve(sketch);
        }
        {
            var Q0;
            Q0 = qSketchRegion(id + "F2", true);
            extrude(context, id + "F3", {"entities" : qUnion([Q0]), "depth" : 20 * mm, "offsetDistance" : 25 * mm});
        }
        {
            var Q0;
            Q0=makeQuery(id+"F3.opExtrude","CAP_FACE",FACE,{"disambiguationData":[OSD([sQuery(id+"F2.wireOp",EDGE,"E2")])],"isStart":false});
            var sketch = newSketch(context, id + "F4", { "sketchPlane" : qUnion([Q0])});
            skCircle(sketch, "E3", {"center": v(-692.22, 0) * mm, "radius": 120 * mm});
            skSolve(sketch);
        }
        {
            var Q0;
            Q0 = qSketchRegion(id + "F4", true);
            extrude(context, id + "F5", {"entities" : qUnion([Q0]), "operationType" : NewBodyOperationType.REMOVE, "oppositeDirection" : true, "depth" : 20 * mm, "offsetDistance" : 25 * mm});
        }
        {
            var Q0;
            Q0=qCreatedBy(makeId("Top.planeOp"),FACE);
            var sketch = newSketch(context, id + "F6", { "sketchPlane" : qUnion([Q0])});
            skCircle(sketch, "E4", {"center": v(-1400, 0) * mm, "radius": 300 * mm});
            skSolve(sketch);
        }
        {
            var Q0;
            Q0=makeQuery(id+"F6.imprint","IMPRINT",FACE,{"disambiguationData":[TD([[makeQuery(id+"F6.imprint","IMPRINT",EDGE,{"derivedFrom":sQuery(id+"F6.wireOp",EDGE,"E4")}),1.0]])]});
            extrude(context, id + "F7", {"entities" : qUnion([Q0]), "depth" : 20 * mm, "offsetDistance" : 25 * mm});
        }
        {
            var Q0;
            Q0=qCreatedBy(makeId("Top.planeOp"),FACE);
            var sketch = newSketch(context, id + "F8", { "sketchPlane" : qUnion([Q0])});
            skCircle(sketch, "E5", {"center": v(-2074.35, 0) * mm, "radius": 120 * mm});
            skCircle(sketch, "E6", {"center": v(-2074.35, 0) * mm, "radius": 110 * mm});
            skSolve(sketch);
        }
        {
            var Q0;
            Q0 = qSketchRegion(id + "F8", true);
            extrude(context, id + "F9", {"entities" : qUnion([Q0]), "depth" : 320 * mm, "offsetDistance" : 25 * mm});
        }
        {
            var Q0;
            Q0=qCreatedBy(makeId("Top.planeOp"),FACE);
            var sketch = newSketch(context, id + "F10", { "sketchPlane" : qUnion([Q0])});
            skLineSegment(sketch, "E7.bottom", {"start": v(-2400.18, -175) * mm, "end": v(-2380.18, -175) * mm});
            skLineSegment(sketch, "E7.top", {"start": v(-2400.18, 175) * mm, "end": v(-2380.18, 175) * mm});
            skLineSegment(sketch, "E7.left", {"start": v(-2400.18, -175) * mm, "end": v(-2400.18, 175) * mm});
            skLineSegment(sketch, "E7.right", {"start": v(-2380.18, -175) * mm, "end": v(-2380.18, 175) * mm});
            skPoint(sketch, "E7.middle", {"position": v(-2390.18, 0) * mm});
            skSolve(sketch);
        }
        {
            var Q0;
            Q0 = qSketchRegion(id + "F10", true);
            extrude(context, id + "F11", {"entities" : qUnion([Q0]), "depth" : 145 * mm, "offsetDistance" : 25 * mm});
        }
        {
            var Q0;
            Q0=qCreatedBy(makeId("Top.planeOp"),FACE);
            var sketch = newSketch(context, id + "F12", { "sketchPlane" : qUnion([Q0])});
            skCircle(sketch, "E8", {"center": v(-2641.06, 0) * mm, "radius": 120 * mm});
            skSolve(sketch);
        }
        {
            var Q0;
            Q0 = qSketchRegion(id + "F12", true);
            extrude(context, id + "F13", {"entities" : qUnion([Q0]), "depth" : 10 * mm, "offsetDistance" : 25 * mm});
        }
        {
            var Q0;
            Q0=qCreatedBy(makeId("Top.planeOp"),FACE);
            var sketch = newSketch(context, id + "F14", { "sketchPlane" : qUnion([Q0])});
            skLineSegment(sketch, "E9.bottom", {"start": v(-3190.95, -150) * mm, "end": v(-2960.95, -150) * mm});
            skLineSegment(sketch, "E9.top", {"start": v(-3190.95, 150) * mm, "end": v(-2960.95, 150) * mm});
            skLineSegment(sketch, "E9.left", {"start": v(-3190.95, -150) * mm, "end": v(-3190.95, 150) * mm});
            skLineSegment(sketch, "E9.right", {"start": v(-2960.95, -150) * mm, "end": v(-2960.95, 150) * mm});
            skPoint(sketch, "E9.middle", {"position": v(-3075.95, 0) * mm});
            skSolve(sketch);
        }
        {
            var Q0;
            Q0 = qSketchRegion(id + "F14", true);
            extrude(context, id + "F15", {"entities" : qUnion([Q0]), "depth" : 7 * mm, "offsetDistance" : 25 * mm});
        }
        {
            var Q0;
            Q0=qCreatedBy(makeId("Top.planeOp"),FACE);
            var sketch = newSketch(context, id + "F16", { "sketchPlane" : qUnion([Q0])});
            skLineSegment(sketch, "E10.bottom", {"start": v(-4045, -80) * mm, "end": v(-3955, -80) * mm});
            skLineSegment(sketch, "E10.top", {"start": v(-4045, 80) * mm, "end": v(-3955, 80) * mm});
            skLineSegment(sketch, "E10.left", {"start": v(-4045, -80) * mm, "end": v(-4045, 80) * mm});
            skLineSegment(sketch, "E10.right", {"start": v(-3955, -80) * mm, "end": v(-3955, 80) * mm});
            skPoint(sketch, "E10.middle", {"position": v(-4000, 0) * mm});
            skCircle(sketch, "E11", {"center": v(-4000, -60) * mm, "radius": 3 * mm});
            skCircle(sketch, "E12", {"center": v(-4000, -70) * mm, "radius": 3 * mm});
            skCircle(sketch, "E13", {"center": v(-4000, 50) * mm, "radius": 7.5 * mm});
            skSolve(sketch);
        }
        {
            var Q0;
            Q0 = qSketchRegion(id + "F16", true);
            extrude(context, id + "F17", {"entities" : qUnion([Q0]), "depth" : 5 * mm, "offsetDistance" : 25 * mm});
        }
        {
            var Q0;
            Q0=qCreatedBy(makeId("Top.planeOp"),FACE);
            var sketch = newSketch(context, id + "F18", { "sketchPlane" : qUnion([Q0])});
            skLineSegment(sketch, "E14.bottom", {"start": v(-4045, 100) * mm, "end": v(-3955, 100) * mm});
            skLineSegment(sketch, "E14.top", {"start": v(-4045, 200) * mm, "end": v(-3955, 200) * mm});
            skLineSegment(sketch, "E14.left", {"start": v(-4045, 100) * mm, "end": v(-4045, 200) * mm});
            skLineSegment(sketch, "E14.right", {"start": v(-3955, 100) * mm, "end": v(-3955, 200) * mm});
            skPoint(sketch, "E14.middle", {"position": v(-4000, 150) * mm});
            skCircle(sketch, "E15", {"center": v(-4000, 190) * mm, "radius": 3 * mm});
            skLineSegment(sketch, "E16.bottom", {"start": v(-3989.54, 180) * mm, "end": v(-3966.96, 180) * mm});
            skLineSegment(sketch, "E16.top", {"start": v(-3989.54, 168) * mm, "end": v(-3966.96, 168) * mm});
            skLineSegment(sketch, "E16.left", {"start": v(-3992.54, 177) * mm, "end": v(-3992.54, 171) * mm});
            skLineSegment(sketch, "E16.right", {"start": v(-3963.96, 177) * mm, "end": v(-3963.96, 171) * mm});
            skPoint(sketch, "E17.visualSharp", {"position": v(-3992.54, 180) * mm});
            skArc(sketch, "E17.filletArc", {"start": v(-3989.54, 180) * mm, "mid": v(-3991.66, 179.12) * mm, "end": v(-3992.54, 177) * mm});
            skPoint(sketch, "E18.visualSharp", {"position": v(-3963.96, 180) * mm});
            skArc(sketch, "E18.filletArc", {"start": v(-3963.96, 177) * mm, "mid": v(-3964.83, 179.12) * mm, "end": v(-3966.96, 180) * mm});
            skPoint(sketch, "E19.visualSharp", {"position": v(-3963.96, 168) * mm});
            skArc(sketch, "E19.filletArc", {"start": v(-3966.96, 168) * mm, "mid": v(-3964.83, 168.88) * mm, "end": v(-3963.96, 171) * mm});
            skPoint(sketch, "E20.visualSharp", {"position": v(-3992.54, 168) * mm});
            skArc(sketch, "E20.filletArc", {"start": v(-3992.54, 171) * mm, "mid": v(-3991.66, 168.88) * mm, "end": v(-3989.54, 168) * mm});
            skSolve(sketch);
        }
        {
            var Q0;
            Q0 = qSketchRegion(id + "F18", true);
            extrude(context, id + "F19", {"entities" : qUnion([Q0]), "depth" : 5 * mm, "offsetDistance" : 25 * mm});
        }
    });
